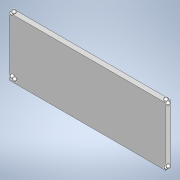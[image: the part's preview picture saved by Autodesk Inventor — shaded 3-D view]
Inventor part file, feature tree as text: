
AUTODESK INVENTOR PART (.ipt)
format: ipt  version: 2020.2 (Build 242310000, 310)  size: 136,704 bytes
history: native  units: in
note: dims shown in document units (in); Inventor stores cm internally (conversion verified against a paired STEP export)
features: sketch x3, extrude x2, hole x2
ambient origin geometry x8: Origin, YZ Plane, XZ Plane, XY Plane, X Axis, Y Axis, Z Axis, Center Point
bodies: Body1 (feature_tree)
feature tree (7):
  sketch  "Sketch1"  dims[d8=47.2441in d9=17.7165in]
  extrude  "Extrusion2"  Depth=17.7165in
  extrude  "Extrusion3"  Depth=1.5748in
  hole  "Hole1"  [1 undecoded]
  hole  "Hole2"  [1 undecoded]
  sketch  "Sketch2"  dims[d10=0.1181in d11=1.5748in]
  sketch  "Sketch3"  dims[d12=0.0in d13=0.1181in d14=0.0in d15=0.15in d16=0.2953in d17=0.1476in d18=0.0984in d19=90.0deg d20=0.3937in d21=0.8108in d22=0.5906in d23=0.5906in d24=0.5906in d25=0.5906in d26=0.5906in d27=0.5906in d28=0.5906in d29=0.5906in d30=0.15in d31=0.2953in d32=0.1476in d33=0.0984in d34=90.0deg d35=0.3937in d36=0.8108in d37=0.0in d38=0.0in d39=0.0in d40=0.0in d41=0.0in d42=0.0in d43=0.0in d44=0.0in]
note: 2 required parameter values undecoded (feature->parameter linkage not recoverable at this tier; creation-order binding heuristic only, values carry confidence <= 0.55)
